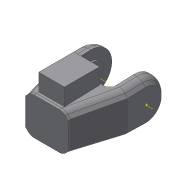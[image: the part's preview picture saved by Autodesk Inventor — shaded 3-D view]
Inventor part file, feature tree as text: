
AUTODESK INVENTOR PART (.ipt)
format: ipt  version: 2018 (Build 220112000, 112)  size: 831,488 bytes
history: native  units: mm
features: sketch x46, projected_geometry x43, extrude x41, other x10, chamfer x6, fillet x5, hole x3, reference x3, mirror x1, plane x1
ambient origin geometry x8: Origin, YZ Plane, XZ Plane, XY Plane, X Axis, Y Axis, Z Axis, Center Point
bodies: Solid1 (feature_tree)
feature tree (159):
  extrude  "Extrusion1"  Depth=45.0mm
  extrude  "Extrusion2"  Depth=2.25mm
  hole  "Hole1"  [1 undecoded]
  hole  "Hole2"  [1 undecoded]
  fillet  "Fillet1"  Radius=14.0mm
  extrude  "Extrusion3"  Depth=5.25mm
  extrude  "Extrusion4"  Depth=10.0mm
  extrude  "Extrusion5"  Depth=2.195mm
  extrude  "Extrusion6"  Depth=8.0mm
  hole  "Hole3"  [1 undecoded]
  extrude  "Extrusion7"  Depth=8.0mm
  extrude  "Extrusion8"  Depth=1.0mm TaperAngle=0.0deg
  extrude  "Extrusion9"  Depth=24.5mm
  extrude  "Extrusion10"  Depth=10.0mm
  extrude  "Extrusion11"  Depth=14.5mm
  extrude  "Extrusion13"  Depth=20.0mm
  extrude  "Extrusion14"  Depth=5.0mm
  extrude  "Extrusion15"  Depth=2.25mm
  extrude  "Extrusion16"  Depth=5.0mm
  extrude  "Extrusion17"  Depth=9.0mm
  chamfer  "Chamfer1"  Distance=1.0mm
  fillet  "Fillet7"  Radius=20.7mm
  fillet  "Fillet8"  Radius=32.0mm
  mirror  "Mirror1"
  sketch  "Sketch26"  dims[d55=2.25mm d56=5.0mm]
  extrude  "Extrusion24"  Depth=1.0mm TaperAngle=0.0deg
  extrude  "Extrusion25"  Depth=8.0mm
  extrude  "Extrusion26"  Depth=0.2mm TaperAngle=0.0deg
  extrude  "Extrusion27"  Depth=8.0mm TaperAngle=0.0deg
  other  "Work Axis1"
  plane  "Work Plane2"
  extrude  "Extrusion28"  Depth=0.2mm TaperAngle=0.0deg
  extrude  "Extrusion29"  Depth=2.5mm TaperAngle=45.0deg
  extrude  "Extrusion31"  Depth=0.5mm
  extrude  "Extrusion32"  Depth=36.0mm
  extrude  "Extrusion33"  Depth=60.0mm
  sketch  "Sketch41"  dims[d100=0.2mm d101=0.0mm d102=2.5mm d103=2.0mm d104=45.0deg]
  extrude  "Extrusion34"  Depth=2.3mm
  chamfer  "Chamfer6"  Distance=15.0mm
  fillet  "Fillet9"  Radius=15.0mm
  extrude  "Extrusion35"  Depth=15.0mm TaperAngle=0.0deg
  extrude  "Extrusion36"  Depth=41.5mm
  fillet  "Fillet10"  Radius=15.5mm
  extrude  "Extrusion37"  Depth=5.0mm
  extrude  "Extrusion38"  Depth=100.0mm TaperAngle=0.0deg
  extrude  "Extrusion40"  Depth=11.5mm
  extrude  "Extrusion41"  Depth=11.5mm
  extrude  "Extrusion42"  Depth=7.0mm
  chamfer  "Chamfer10"  Distance=100.0mm
  chamfer  "Chamfer11"  Distance=100.0mm
  chamfer  "Chamfer12"  Distance=100.0mm
  chamfer  "Chamfer13"  Distance=5.0mm Angle=45.0deg
  sketch  "Sketch61"  dims[d172=0.0mm d173=11.5mm]
  sketch  "Sketch62"  dims[d175=11.5mm d176=11.5mm]
  extrude  "Extrusion47"  TaperAngle=15.0deg  [1 undecoded]
  extrude  "Extrusion48"  Depth=15.470628mm
  extrude  "Extrusion49"  Depth=1.0mm TaperAngle=0.0deg
  extrude  "Extrusion50"  TaperAngle=15.0deg  [1 undecoded]
  extrude  "Extrusion51"  Depth=10.0mm
  extrude  "Extrusion52"  Depth=10.0mm TaperAngle=0.0deg
  extrude  "Extrusion53"  Depth=10.0mm
  extrude  "Extrusion54"  Depth=10.0mm TaperAngle=0.0deg
  sketch  "Sketch1"  dims[d0=24.5mm d1=45.0mm]
  sketch  "Sketch2"  dims[d2=1.95mm d3=0.0mm d4=2.25mm]
  projected_geometry  "Projected Loop1"
  sketch  "Sketch3"  dims[d5=20.0mm d6=2.25mm]
  projected_geometry  "Projected Loop2"
  sketch  "Sketch4"  dims[d7=5.25mm d8=5.25mm d9=14.0mm]
  projected_geometry  "Projected Loop3"
  sketch  "Sketch5"  dims[d10=5.25mm d11=18.5mm]
  projected_geometry  "Projected Loop4"
  sketch  "Sketch6"  dims[d12=10.0mm d13=0.0mm d14=20.5mm]
  projected_geometry  "Projected Loop5"
  sketch  "Sketch7"  dims[d15=2.0mm d16=2.195mm]
  projected_geometry  "Projected Loop6"
  sketch  "Sketch8"  dims[d17=2.0mm]
  projected_geometry  "Projected Loop7"
  sketch  "Sketch9"  dims[d18=2.4mm d19=6.0mm d20=4.4mm d21=2.0mm d22=90.0deg d23=8.0mm d24=20.594885mm d25=20.5mm]
  projected_geometry  "Projected Loop8"
  projected_geometry  "Projected Loop9"
  sketch  "Sketch10"  dims[d26=26.65mm d27=2.0mm]
  projected_geometry  "Projected Loop10"
  projected_geometry  "Projected Loop11"
  sketch  "Sketch11"  dims[d28=2.0mm]
  projected_geometry  "Projected Loop12"
  sketch  "Sketch12"  dims[d29=2.4mm d30=6.0mm d31=4.4mm d32=2.0mm d33=90.0deg d34=8.0mm d35=20.594885mm d36=0.5mm]
  sketch  "Sketch13"  dims[d37=18.0mm d38=1.0mm d39=0.0mm]
  sketch  "Sketch14"  dims[d41=5.0mm d42=0.0mm d43=24.5mm]
  projected_geometry  "Projected Loop13"
  sketch  "Sketch16"  dims[d44=1.15mm d45=0.0mm d46=10.0mm]
  projected_geometry  "Projected Loop14"
  sketch  "Sketch17"  dims[d47=21.0mm d48=14.5mm]
  projected_geometry  "Projected Loop15"
  sketch  "Sketch18"  dims[d49=20.0mm d50=14.5mm]
  projected_geometry  "Projected Loop16"
  sketch  "Sketch19"  dims[d51=24.5mm d52=5.0mm]
  projected_geometry  "Projected Loop17"
  sketch  "Sketch20"  dims[d53=5.0mm d54=2.25mm]
  projected_geometry  "Projected Loop18"
  projected_geometry  "Projected Loop25"
  sketch  "Sketch31"  dims[d57=5.0mm d58=9.0mm]
  projected_geometry  "Projected Loop30"
  reference  "Reference1"
  sketch  "Sketch32"  dims[d59=14.75mm]
  projected_geometry  "Projected Loop31"
  sketch  "Sketch33"  dims[d60=4.0mm d61=1.0mm d62=0.0mm d63=20.7mm]
  projected_geometry  "Projected Loop32"
  sketch  "Sketch34"  dims[d64=2.3mm d65=6.0mm d66=4.4mm d67=2.0mm d68=90.0deg d69=8.0mm d70=20.594885mm d72=32.0mm]
  projected_geometry  "Projected Loop33"
  other  "Work Point1"
  other  "Work Point2"
  other  "Work Point3"
  sketch  "Sketch35"  dims[d73=3.0mm d74=0.0mm d75=1.0mm d76=0.0mm]
  sketch  "Sketch37"  dims[d77=12.25mm d78=0.0mm d80=8.0mm]
  projected_geometry  "Projected Loop34"
  sketch  "Sketch38"  dims[d81=4.5mm d82=0.0mm d84=0.2mm d85=0.0mm]
  sketch  "Sketch39"  dims[d91=8.0mm d92=0.0mm d93=5.0mm d94=0.0mm]
  sketch  "Sketch40"  dims[d95=5.0mm d96=0.0mm d98=0.2mm d99=0.0mm]
  projected_geometry  "Projected Loop35"
  projected_geometry  "Projected Loop36"
  projected_geometry  "Projected Loop37"
  projected_geometry  "Projected Loop38"
  sketch  "Sketch42"  dims[d105=1.5mm d114=0.5mm]
  projected_geometry  "Projected Loop39"
  sketch  "Sketch43"  dims[d130=60.0mm d131=36.0mm]
  reference  "Reference2"
  reference  "Reference3"
  sketch  "Sketch45"  dims[d146=40.0mm d147=60.0mm]
  projected_geometry  "Projected Loop40"
  sketch  "Sketch46"  dims[d148=0.0mm d149=2.3mm d150=15.0mm d151=0.0mm d152=15.0mm d153=0.0mm]
  projected_geometry  "Projected Loop41"
  sketch  "Sketch48"  dims[d154=15.0mm d155=0.0mm d156=15.0mm d157=0.0mm]
  projected_geometry  "Projected Loop43"
  sketch  "Sketch50"  dims[d158=20.5mm d159=41.5mm d160=15.5mm]
  projected_geometry  "Projected Loop46"
  sketch  "Sketch53"  dims[d161=15.5mm d162=5.0mm]
  projected_geometry  "Projected Loop47"
  sketch  "Sketch55"  dims[d165=100.0mm d166=0.0mm d167=100.0mm d168=0.0mm]
  projected_geometry  "Projected Loop60"
  sketch  "Sketch63"  dims[d179=100.0mm d180=0.0mm d187=7.0mm d188=100.0mm d189=0.0mm d193=100.0mm d194=0.0mm d195=100.0mm d196=0.0mm d197=5.0mm d198=2.0mm d199=45.0deg]
  projected_geometry  "Projected Loop61"
  sketch  "Sketch64"  dims[d200=8.0mm d202=15.0deg]
  projected_geometry  "Projected Loop62"
  sketch  "Sketch65"  dims[d204=10.970628mm d205=15.470628mm]
  projected_geometry  "Projected Loop63"
  sketch  "Sketch66"  dims[d206=1.0mm d207=0.0mm d208=1.0mm d209=0.0mm]
  projected_geometry  "Projected Loop64"
  sketch  "Sketch67"  dims[d213=2.0mm d215=15.0deg]
  projected_geometry  "Projected Loop65"
  sketch  "Sketch68"  dims[d216=4.0mm d217=4.0mm d218=5.0mm d219=0.0mm d222=32.0mm d223=4.0mm d224=0.0mm d227=6.5mm d228=0.0mm d244=20.5mm d245=3.05mm d246=0.0mm d255=20.5mm d256=1.55mm d257=0.0mm d330=3.0mm d331=2.0mm d332=45.0deg d333=4.5mm d334=20.0mm d335=45.0deg d336=5.0mm d337=20.0mm d338=45.0deg d339=5.0mm d340=20.0mm d341=45.0deg d361=10.0mm d362=0.0mm d363=2.0mm d364=51.5mm d365=0.0mm d366=45.0mm d367=0.0mm d368=3.0mm d369=0.0mm d370=51.5mm d371=0.0mm d372=51.5mm d373=0.0mm d374=51.5mm d375=0.0mm d376=51.5mm d377=0.0mm d378=51.5mm d379=0.0mm]
  projected_geometry  "Projected Loop66"
  parser-record x1  (decoder bookkeeping rows leaked as tree rows — omitted from the tree; the rows remain in map.json)
  other  "servocheck.iam"
  other  "LX-16A:3"
  other  "DUOPAN-SG-SJ_10"
  projected_geometry  "Project Cut Edges1"
  projected_geometry  "Project Cut Edges3"
  other  "bottomarm:1"
  other  "arm1:1"
note: 5 required parameter values undecoded (feature->parameter linkage not recoverable at this tier; creation-order binding heuristic only, values carry confidence <= 0.55)
note: 1 file-system path scrubbed to <path> (originals preserved in map.json)
